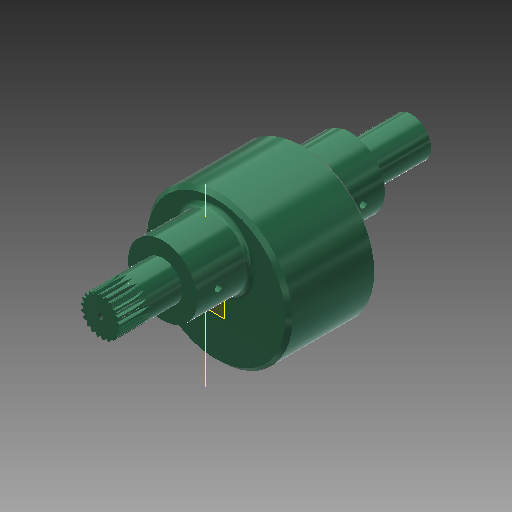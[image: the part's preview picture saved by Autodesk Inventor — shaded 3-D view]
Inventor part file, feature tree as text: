
AUTODESK INVENTOR PART (.ipt)
format: ipt  version: 2019 (Build 230136000, 136)  size: 605,696 bytes
history: native  units: mm (DEFAULTED — no unit token found)
features: sketch x10, extrude x8, revolve x2, other x2, plane x1, fillet x1, chamfer x1, hole x1, thread x1, projected_geometry x1
ambient origin geometry x8: Origin, YZ Plane, XZ Plane, XY Plane, X Axis, Y Axis, Z Axis, Center Point
bodies: Solid1 (feature_tree)
feature tree (28):
  extrude  "Extrusion1"  Depth=24.0mm TaperAngle=0.0deg
  extrude  "Extrusion5"  Depth=14.354mm
  extrude  "Extrusion6"  Depth=30.0mm TaperAngle=0.0deg
  revolve  "Revolution1"  [1 undecoded]
  extrude  "Extrusion7"  Depth=20.0mm
  plane  "Work Plane2"
  extrude  "Extrusion8"  Depth=6.0mm
  fillet  "Fillet4"  Radius=15.0mm
  chamfer  "Chamfer3"  Distance=6.0mm
  extrude  "Extrusion9"  Depth=2.0mm TaperAngle=45.0deg
  extrude  "Extrusion10"  Depth=11.0mm
  other  "Involute Splining1"
  hole  "Hole1"  [1 undecoded]
  extrude  "Extrusion11"  Depth=11.0mm TaperAngle=0.0deg
  thread  "Thread1"  [1 undecoded]
  revolve  "Revolution2"  [1 undecoded]
  sketch  "Sketch1"  dims[d1=39.0mm d3=24.0mm d4=0.0mm]
  sketch  "Sketch5"  dims[d22=82.0mm d23=14.354mm]
  sketch  "Sketch6"  dims[d24=56.0mm d25=0.0mm d26=30.0mm d27=0.0mm]
  sketch  "Sketch7"  dims[d32=35.0mm d33=11.0mm]
  sketch  "Sketch8"  dims[d34=90.0deg d37=20.0mm]
  sketch  "Sketch9"  dims[d39=4.0mm d40=0.0mm d41=6.0mm d42=15.0mm]
  sketch  "Sketch10"  dims[d43=6.0mm]
  sketch  "Sketch11"  dims[d44=90.0mm]
  projected_geometry  "Projected Loop1"
  other  "Shaft Groove"
  sketch  "Sketch12"  dims[d45=39.0mm d46=6.0mm d47=0.0mm]
  sketch  "Sketch13"  dims[d48=3.0mm d49=2.0mm d50=2.0mm d51=45.0deg d52=20.0mm d53=30.0mm d54=0.0mm d55=4.5mm d56=0.0mm d57=10.0mm d58=10.0mm d59=3.242mm d60=8.0mm d61=4.0mm d62=2.0mm d63=90.0deg d64=8.0mm d65=20.594885mm d66=4.0mm d67=12.0mm d68=12.0mm d69=0.0mm d70=0.0mm d71=10.0mm d72=0.0mm d75=35.0mm d76=0.0mm d77=11.0mm d78=3.0mm d79=90.0deg]
note: 4 required parameter values undecoded (feature->parameter linkage not recoverable at this tier; creation-order binding heuristic only, values carry confidence <= 0.55)